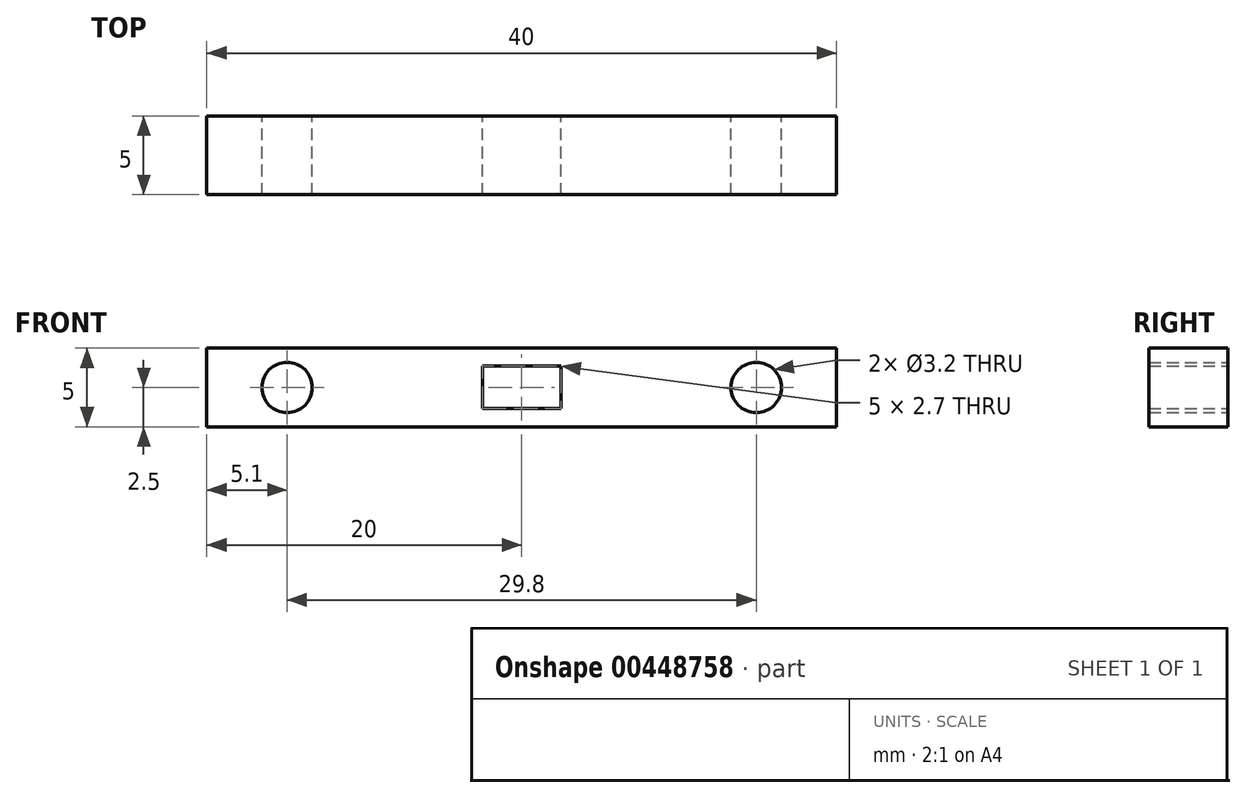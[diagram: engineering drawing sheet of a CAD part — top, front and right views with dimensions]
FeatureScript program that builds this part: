
annotation { "Feature Type Name" : "Feature", "Feature Type Description" : "" }
export const myFeature = defineFeature(function(context is Context, id is Id, definition is map)
    precondition{}
    {
        {
            var Q0;
            Q0=qCreatedBy(makeId("Front.planeOp"),FACE);
            var sketch = newSketch(context, id + "F0", { "sketchPlane" : qUnion([Q0])});
            skLineSegment(sketch, "E0.bottom", {"start": v(20, 2.5) * mm, "end": v(-20, 2.5) * mm});
            skLineSegment(sketch, "E0.top", {"start": v(20, -2.5) * mm, "end": v(-20, -2.5) * mm});
            skLineSegment(sketch, "E0.left", {"start": v(20, 2.5) * mm, "end": v(20, -2.5) * mm});
            skLineSegment(sketch, "E0.right", {"start": v(-20, 2.5) * mm, "end": v(-20, -2.5) * mm});
            skPoint(sketch, "E0.middle", {"position": v(0, 0) * mm});
            skCircle(sketch, "E1", {"center": v(-14.9, 0) * mm, "radius": 1.6 * mm});
            skLineSegment(sketch, "E2", {"start": v(0, 2.5) * mm, "end": v(0, -2.5) * mm, "construction": true});
            skCircle(sketch, "E3.MirrorC", {"center": v(14.9, 0) * mm, "radius": 1.6 * mm});
            skLineSegment(sketch, "E4.bottom", {"start": v(2.5, 1.35) * mm, "end": v(-2.5, 1.35) * mm});
            skLineSegment(sketch, "E4.top", {"start": v(2.5, -1.35) * mm, "end": v(-2.5, -1.35) * mm});
            skLineSegment(sketch, "E4.left", {"start": v(2.5, 1.35) * mm, "end": v(2.5, -1.35) * mm});
            skLineSegment(sketch, "E4.right", {"start": v(-2.5, 1.35) * mm, "end": v(-2.5, -1.35) * mm});
            skSolve(sketch);
        }
        {
            var Q0;
            Q0=qSketchRegion(id+"F0",true);
            extrude(context, id + "F1", {"entities" : qUnion([Q0]), "depth" : 5 * mm});
        }
    });
